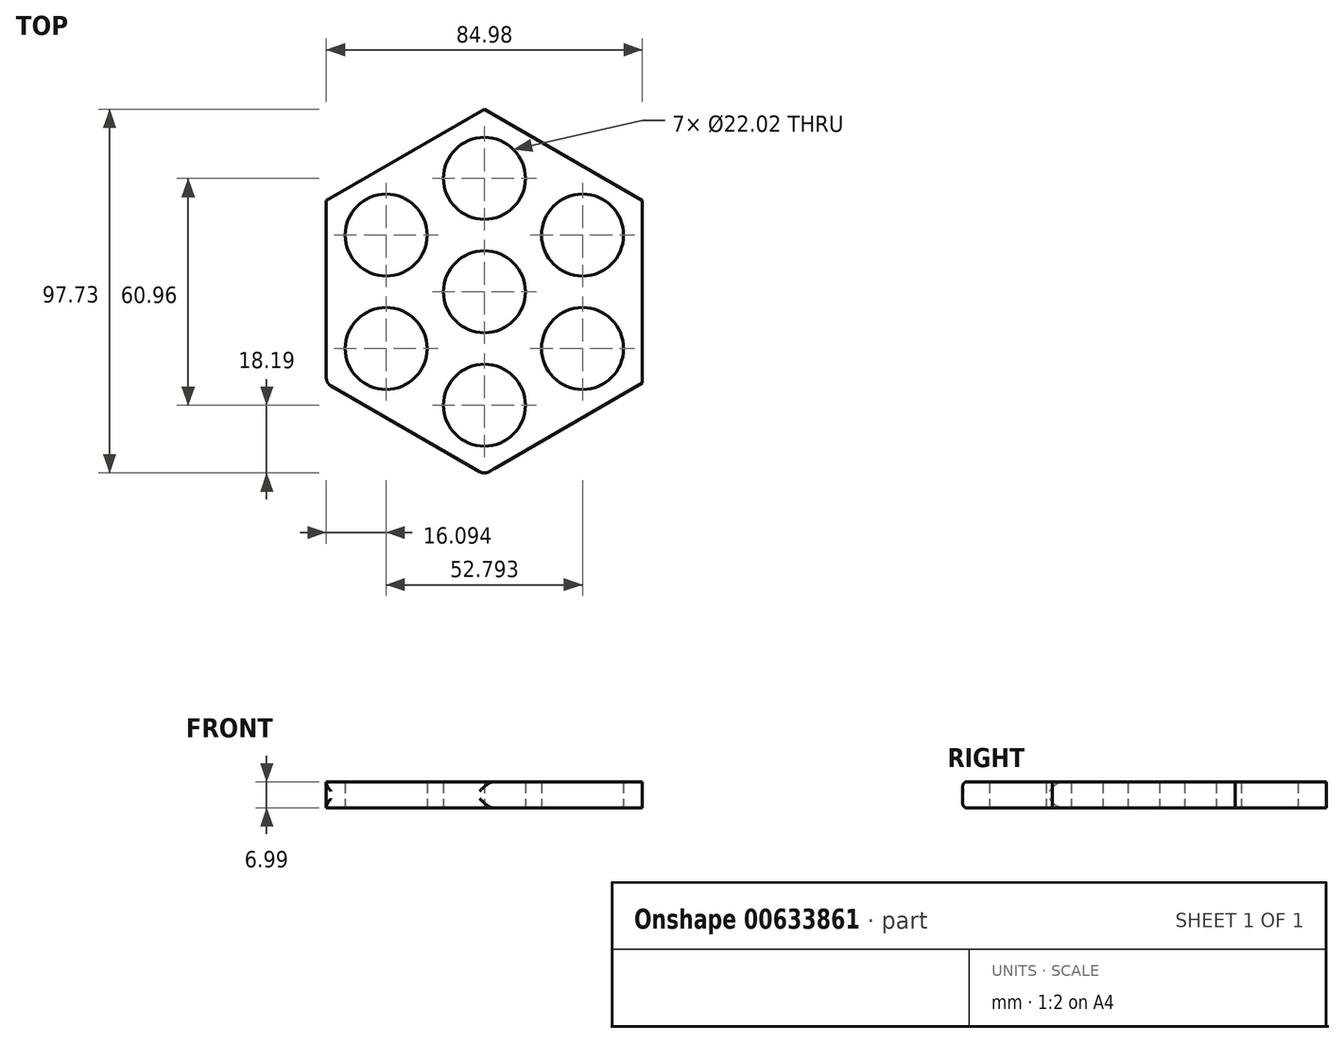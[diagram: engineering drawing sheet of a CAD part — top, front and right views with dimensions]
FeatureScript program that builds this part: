
annotation { "Feature Type Name" : "Feature", "Feature Type Description" : "" }
export const myFeature = defineFeature(function(context is Context, id is Id, definition is map)
    precondition{}
    {
        {
            var Q0;
            Q0=qCreatedBy(makeId("Top.planeOp"),FACE);
            var sketch = newSketch(context, id + "F0", { "sketchPlane" : qUnion([Q0])});
            skCircle(sketch, "E0", {"center": v(0, 0) * mm, "radius": 11.01 * mm});
            skLineSegment(sketch, "E1", {"start": v(0, 0) * mm, "end": v(0, 30.48) * mm});
            skLineSegment(sketch, "E2", {"start": v(0, 0) * mm, "end": v(26.4, 15.24) * mm});
            skLineSegment(sketch, "E3", {"start": v(0, 0) * mm, "end": v(26.4, -15.24) * mm});
            skLineSegment(sketch, "E4", {"start": v(0, 0) * mm, "end": v(0, -30.48) * mm});
            skLineSegment(sketch, "E5", {"start": v(0, 0) * mm, "end": v(-26.4, -15.24) * mm});
            skLineSegment(sketch, "E6", {"start": v(0, 0) * mm, "end": v(-26.4, 15.24) * mm});
            skCircle(sketch, "E7", {"center": v(-26.4, 15.24) * mm, "radius": 11.01 * mm});
            skCircle(sketch, "E8", {"center": v(0, 30.48) * mm, "radius": 11.01 * mm});
            skCircle(sketch, "E9", {"center": v(26.4, 15.24) * mm, "radius": 11.01 * mm});
            skCircle(sketch, "E10", {"center": v(26.4, -15.24) * mm, "radius": 11.01 * mm});
            skCircle(sketch, "E11", {"center": v(0, -30.48) * mm, "radius": 11.01 * mm});
            skCircle(sketch, "E12", {"center": v(-26.4, -15.24) * mm, "radius": 11.01 * mm});
            skCircle(sketch, "E13.cCircle", {"center": v(0, 0) * mm, "radius": 49.06 * mm, "construction": true});
            skLineSegment(sketch, "E13.0", {"start": v(0, -49.06) * mm, "end": v(-42.49, -24.53) * mm});
            skLineSegment(sketch, "E13.1", {"start": v(-42.49, -24.53) * mm, "end": v(-42.49, 24.53) * mm});
            skLineSegment(sketch, "E13.2", {"start": v(-42.49, 24.53) * mm, "end": v(0, 49.06) * mm});
            skLineSegment(sketch, "E13.3", {"start": v(0, 49.06) * mm, "end": v(42.49, 24.53) * mm});
            skLineSegment(sketch, "E13.4", {"start": v(42.49, 24.53) * mm, "end": v(42.49, -24.53) * mm});
            skLineSegment(sketch, "E13.5", {"start": v(42.49, -24.53) * mm, "end": v(0, -49.06) * mm});
            skSolve(sketch);
        }
        {
            var Q0;
            Q0 = qSketchRegion(id + "F0", true);
            extrude(context, id + "F1", {"entities" : qUnion([Q0]), "depth" : 7 * mm, "offsetDistance" : 25.4 * mm});
        }
        {
            var Q0;
            Q0=makeQuery(id+"F1.opExtrude","SWEPT_FACE",FACE,{"disambiguationData":[OSD([sQuery(id+"F0.wireOp",EDGE,"E13.0")])]});
            fillet(context, id + "F2", {"entities" : qUnion([Q0]), "radius" : 2.54 * mm, "tangentPropagation" : true, "allowEdgeOverflow" : false});
        }
    });
